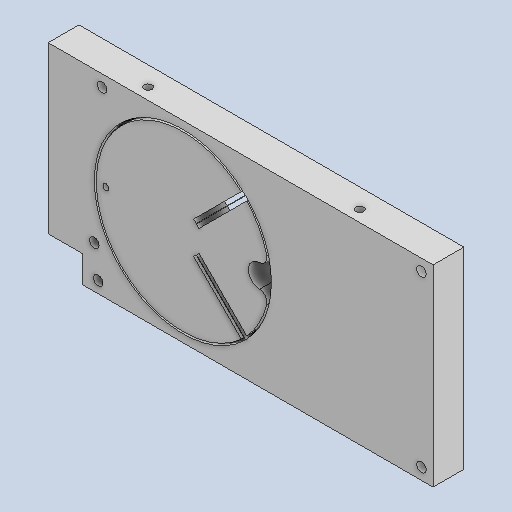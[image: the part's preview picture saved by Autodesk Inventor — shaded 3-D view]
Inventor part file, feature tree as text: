
AUTODESK INVENTOR PART (.ipt)
format: ipt  version: 2023 (Build 270158000, 158)  size: 279,552 bytes
history: native  units: mm
features: extrude x7, sketch x7, other x6, reference x6, fillet x1
ambient origin geometry x8: Origin, YZ Plane, XZ Plane, XY Plane, X Axis, Y Axis, Z Axis, Center Point
bodies: Solid1 (feature_tree)
feature tree (27):
  other  "<userpath>\ClawdDrive\Objet3D\IminaProbe\V3Roue\Settings.xlsx"
  extrude  "Extrusion1"  Depth=100.0mm
  extrude  "Extrusion4"  Depth=5.0mm
  fillet  "Fillet2"  Radius=5.0mm
  extrude  "Extrusion5"  Depth=5.0mm
  extrude  "Extrusion6"  Depth=15.0mm
  extrude  "Extrusion7"  Depth=3.5mm
  extrude  "Extrusion8"  Depth=3.5mm
  extrude  "Extrusion9"  Depth=10.0mm TaperAngle=0.0deg
  sketch  "Sketch1"  dims[d0=50.0mm d1=100.0mm]
  sketch  "Sketch4"  dims[d2=5.0mm d3=5.0mm d4=5.0mm]
  sketch  "Sketch5"  dims[d5=5.0mm d6=5.0mm]
  sketch  "Sketch6"  dims[d7=15.0mm d8=15.0mm]
  reference  "Reference4"
  reference  "Reference5"
  sketch  "Sketch7"  dims[d9=5.0mm d10=3.5mm]
  reference  "Reference6"
  reference  "Reference7"
  reference  "Reference9"
  reference  "Reference10"
  sketch  "Sketch8"  dims[d11=3.5mm d12=3.5mm]
  sketch  "Sketch9"  dims[d13=3.5mm d14=8.0mm d15=0.0mm d22=15.0mm d23=40.0mm d24=20.0mm d25=45.0mm d26=1.6mm d27=6.0mm d28=45.0deg d29=45.0deg d30=46.0mm d31=25.0mm d32=25.0mm d33=25.0mm d34=10.0mm d35=1.0mm d36=1.0mm d37=0.1mm d38=0.05mm d39=0.1mm d40=0.05mm d41=1.0mm d42=1.0mm d43=8.0mm d44=0.0mm d46=2.0mm d47=15.0mm d48=1.5mm d49=9.0mm d50=0.0mm d51=7.0mm d52=1.6mm d53=1.6mm d54=8.0mm d55=0.0mm d56=2.5mm d57=2.5mm d58=2.5mm d59=2.5mm d60=2.5mm d61=8.0mm d62=0.0mm d63=2.5mm d64=3.0mm d65=4.0mm d66=8.0mm d67=0.0mm d68=2.05mm d69=2.05mm d70=2.05mm d71=2.05mm d72=8.0mm d73=0.0mm d74=23.0mm d75=23.0mm d76=55.0mm d77=23.0mm d78=55.0mm]
  other  "<userpath>\ClawdDrive\Objet3D\IminaProbe\V3Roue\RoueV3.iam"
  other  "RoueV3.iam"
  other  "CapacitiveSensor:1"
  other  "RoueV3PartB:1"
  other  "RoueV3PartC:1"
